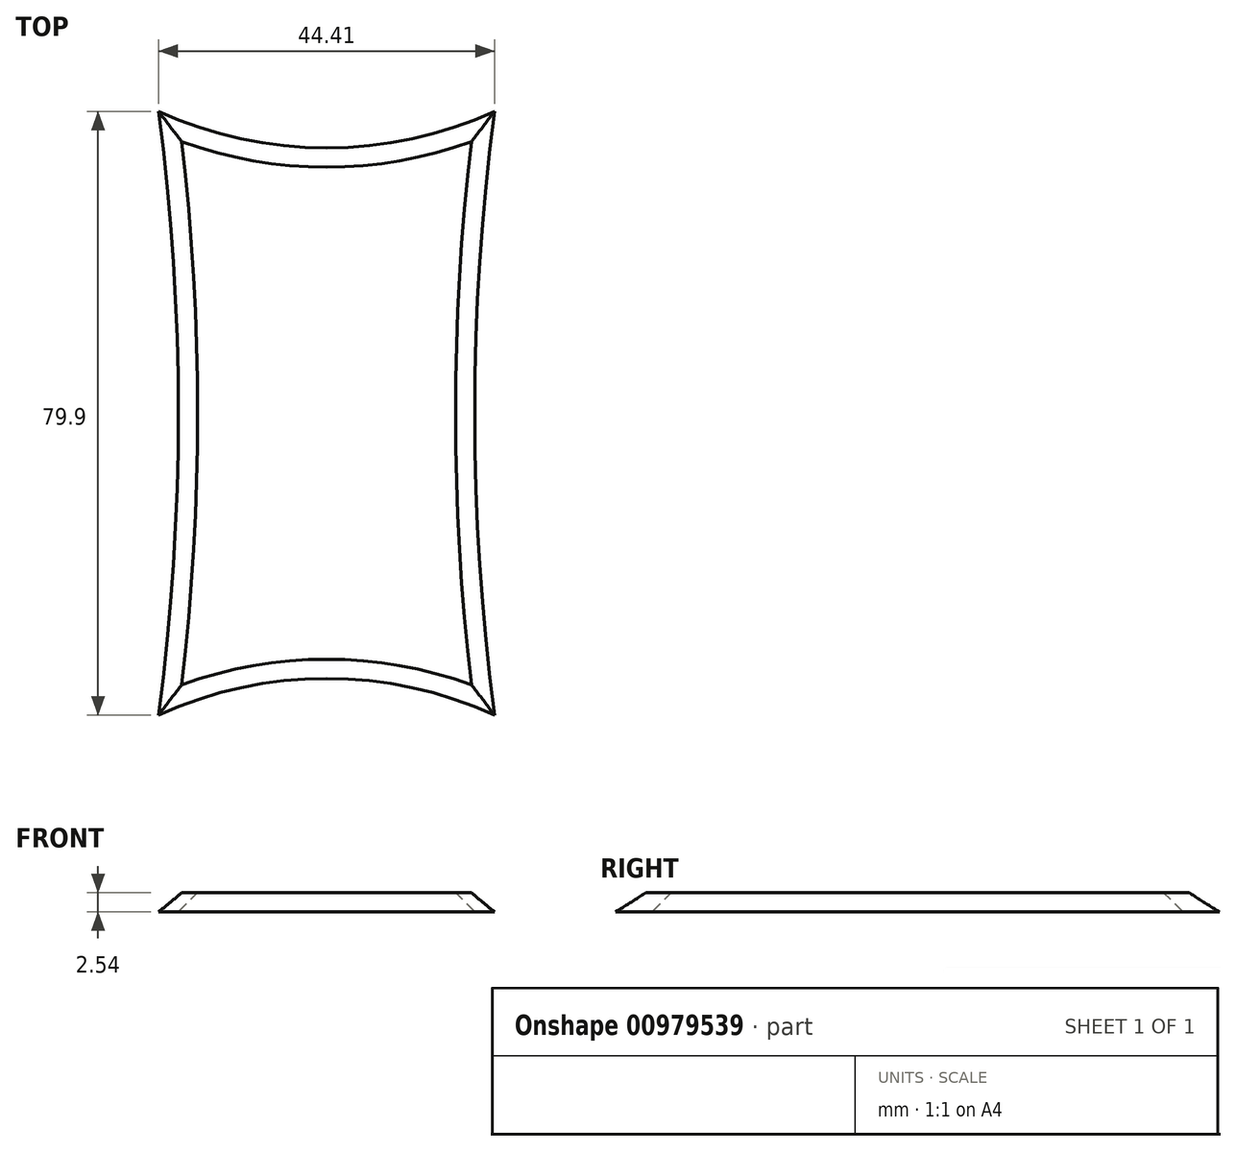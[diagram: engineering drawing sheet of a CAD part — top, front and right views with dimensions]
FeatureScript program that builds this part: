
annotation { "Feature Type Name" : "Feature", "Feature Type Description" : "" }
export const myFeature = defineFeature(function(context is Context, id is Id, definition is map)
    precondition{}
    {
        {
            var Q0;
            Q0=qCreatedBy(makeId("Top.planeOp"),FACE);
            var sketch = newSketch(context, id + "F0", { "sketchPlane" : qUnion([Q0])});
            skLineSegment(sketch, "E0.bottom", {"start": v(-10.21, 8.66) * mm, "end": v(-61.01, 8.66) * mm});
            skLineSegment(sketch, "E0.top", {"start": v(-10.21, 97.56) * mm, "end": v(-61.01, 97.56) * mm});
            skLineSegment(sketch, "E0.left", {"start": v(-10.21, 8.66) * mm, "end": v(-10.21, 97.56) * mm});
            skLineSegment(sketch, "E0.right", {"start": v(-61.01, 8.66) * mm, "end": v(-61.01, 97.56) * mm});
            skPoint(sketch, "E0.middle", {"position": v(-35.61, 53.11) * mm});
            skArc(sketch, "E1", {"start": v(-10.21, 8.66) * mm, "mid": v(-35.61, 15.47) * mm, "end": v(-61.01, 8.66) * mm});
            skArc(sketch, "E2", {"start": v(-10.21, 97.56) * mm, "mid": v(-13.47, 53.11) * mm, "end": v(-10.21, 8.66) * mm});
            skArc(sketch, "E3", {"start": v(-61.01, 97.56) * mm, "mid": v(-35.61, 90.76) * mm, "end": v(-10.21, 97.56) * mm});
            skArc(sketch, "E4", {"start": v(-61.01, 8.66) * mm, "mid": v(-57.76, 53.11) * mm, "end": v(-61.01, 97.56) * mm});
            skSolve(sketch);
        }
        {
            var Q0;
            Q0=makeQuery(id+"F0.imprint","IMPRINT",FACE,{"disambiguationData":[TD([[makeQuery(id+"F0.imprint","IMPRINT",EDGE,{"derivedFrom":sQuery(id+"F0.wireOp",EDGE,"E1")}),-1.0]])]});
            extrude(context, id + "F1", {"entities" : qUnion([Q0]), "depth" : 2.54 * mm, "offsetDistance" : 25.4 * mm});
        }
        {
            var Q0;
            Q0=makeQuery(id+"F1.opExtrude","CAP_EDGE",EDGE,{"disambiguationData":[OSD([sQuery(id+"F0.wireOp",EDGE,"E4")])],"isStart":false});
            var Q1;
            Q1=makeQuery(id+"F1.opExtrude","CAP_EDGE",EDGE,{"disambiguationData":[OSD([sQuery(id+"F0.wireOp",EDGE,"E1")])],"isStart":false});
            var Q2;
            Q2=makeQuery(id+"F1.opExtrude","CAP_EDGE",EDGE,{"disambiguationData":[OSD([sQuery(id+"F0.wireOp",EDGE,"E2")])],"isStart":false});
            var Q3;
            Q3=makeQuery(id+"F1.opExtrude","CAP_EDGE",EDGE,{"disambiguationData":[OSD([sQuery(id+"F0.wireOp",EDGE,"E3")])],"isStart":false});
            chamfer(context, id + "F2", {"entities" : qUnion([Q0, Q1, Q2, Q3]), "width" : 5.08 * mm, "tangentPropagation" : true});
        }
    });
